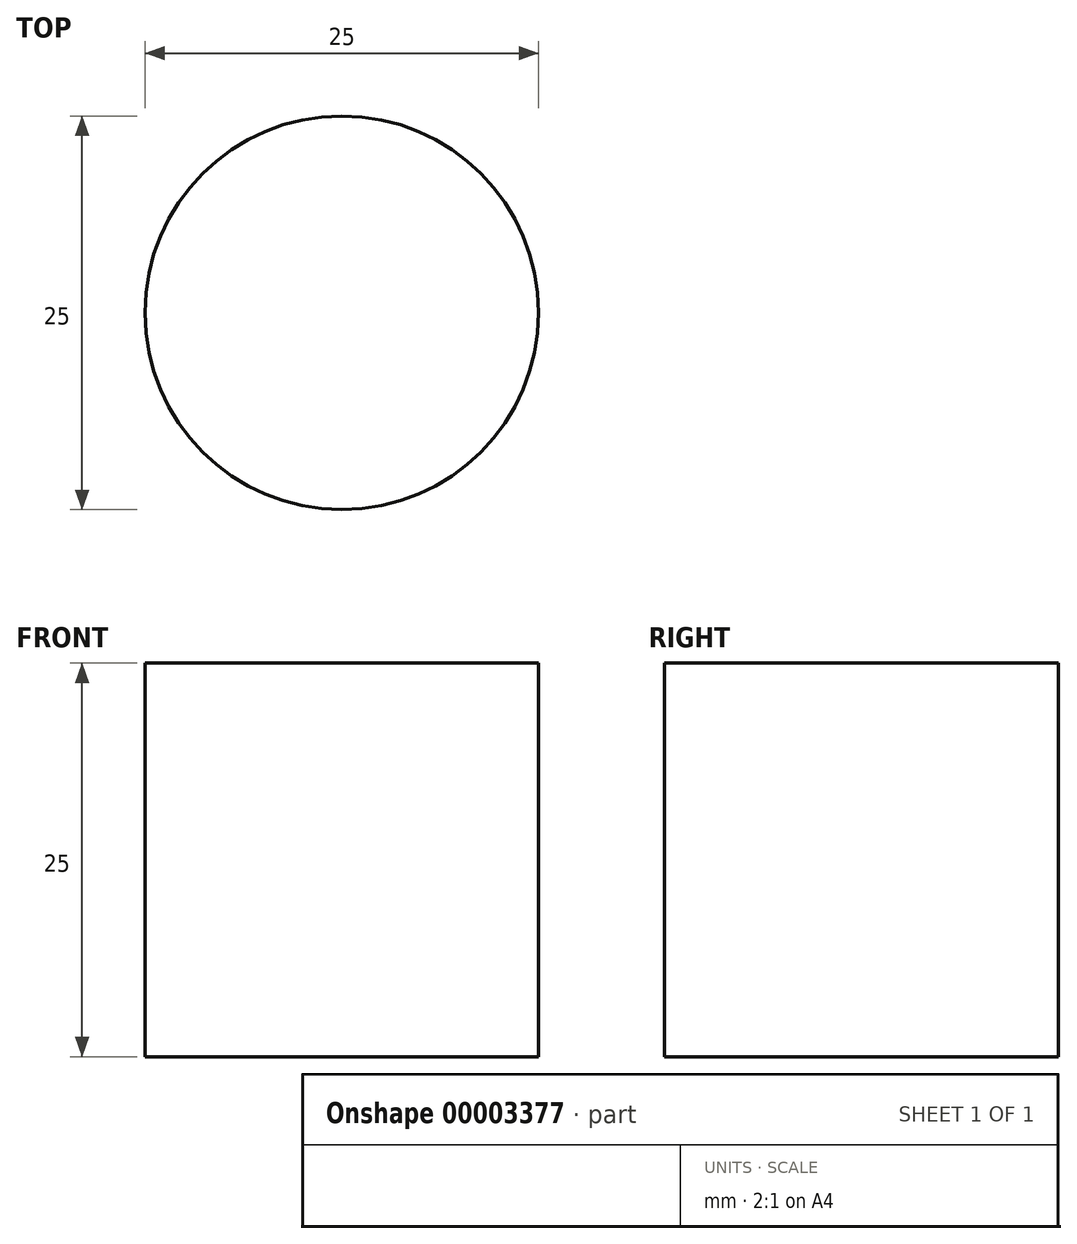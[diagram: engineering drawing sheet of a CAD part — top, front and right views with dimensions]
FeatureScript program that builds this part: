
annotation { "Feature Type Name" : "Feature", "Feature Type Description" : "" }
export const myFeature = defineFeature(function(context is Context, id is Id, definition is map)
    precondition{}
    {
        {
            var Q0;
            Q0=qCreatedBy(makeId("Top.planeOp"),FACE);
            var sketch = newSketch(context, id + "F0", { "sketchPlane" : qUnion([Q0])});
            skCircle(sketch, "E0", {"center": v(0, 0) * mm, "radius": 12.5 * mm});
            skSolve(sketch);
        }
        {
            var Q0;
            Q0=makeQuery(id+"F0.imprint","IMPRINT",FACE,{"disambiguationData":[TD([[makeQuery(id+"F0.imprint","IMPRINT",EDGE,{"derivedFrom":sQuery(id+"F0.wireOp",EDGE,"E0")}),1.0]])]});
            extrude(context, id + "F1", {"entities" : qUnion([Q0]), "depth" : 25 * mm});
        }
    });
